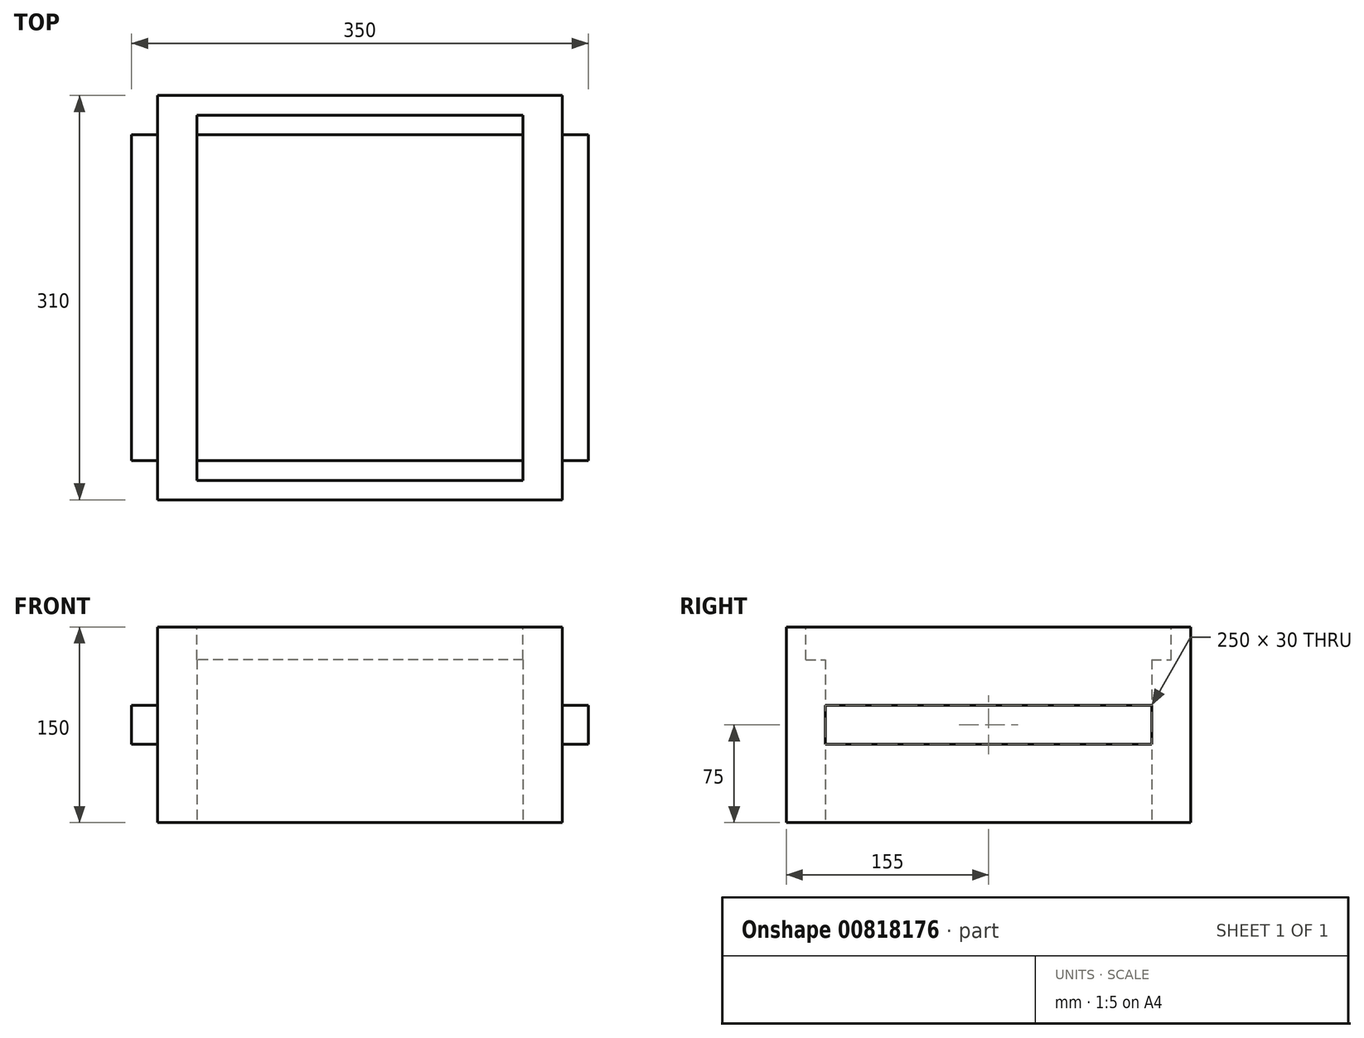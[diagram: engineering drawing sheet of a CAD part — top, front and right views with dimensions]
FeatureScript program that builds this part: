
annotation { "Feature Type Name" : "Feature", "Feature Type Description" : "" }
export const myFeature = defineFeature(function(context is Context, id is Id, definition is map)
    precondition{}
    {
        {
            var Q0;
            Q0=qCreatedBy(makeId("Top.planeOp"),FACE);
            var sketch = newSketch(context, id + "F0", { "sketchPlane" : qUnion([Q0])});
            skLineSegment(sketch, "E0.bottom", {"start": v(125, -125) * mm, "end": v(-125, -125) * mm});
            skLineSegment(sketch, "E0.top", {"start": v(125, 125) * mm, "end": v(-125, 125) * mm});
            skLineSegment(sketch, "E0.left", {"start": v(125, -125) * mm, "end": v(125, 125) * mm});
            skLineSegment(sketch, "E0.right", {"start": v(-125, -125) * mm, "end": v(-125, 125) * mm});
            skPoint(sketch, "E0.middle", {"position": v(0, 0) * mm});
            skLineSegment(sketch, "E1.bottom", {"start": v(155, -155) * mm, "end": v(-155, -155) * mm});
            skLineSegment(sketch, "E1.top", {"start": v(155, 155) * mm, "end": v(-155, 155) * mm});
            skLineSegment(sketch, "E1.left", {"start": v(155, -155) * mm, "end": v(155, 155) * mm});
            skLineSegment(sketch, "E1.right", {"start": v(-155, -155) * mm, "end": v(-155, 155) * mm});
            skSolve(sketch);
        }
        {
            var Q0;
            Q0=makeQuery(id+"F0.imprint","IMPRINT",FACE,{"disambiguationData":[TD([[makeQuery(id+"F0.imprint","IMPRINT",EDGE,{"derivedFrom":sQuery(id+"F0.wireOp",EDGE,"E0.bottom")}),1.0]])]});
            extrude(context, id + "F1", {"entities" : qUnion([Q0]), "endBound" : BoundingType.SYMMETRIC, "depth" : 150 * mm, "offsetDistance" : 25.4 * mm});
        }
        {
            var Q0;
            Q0=makeQuery(id+"F1.opExtrude","CAP_FACE",FACE,{"disambiguationData":[OSD([sQuery(id+"F0.wireOp",EDGE,"E0.bottom"),sQuery(id+"F0.wireOp",EDGE,"E0.top"),sQuery(id+"F0.wireOp",EDGE,"E0.left"),sQuery(id+"F0.wireOp",EDGE,"E0.right"),sQuery(id+"F0.wireOp",EDGE,"E1.bottom"),sQuery(id+"F0.wireOp",EDGE,"E1.top"),sQuery(id+"F0.wireOp",EDGE,"E1.left"),sQuery(id+"F0.wireOp",EDGE,"E1.right")])],"isStart":false});
            cPlane(context, id + "F2", {"entities" : qUnion([Q0]), "cplaneType" : CPlaneType.OFFSET, "offset" : 0 * mm, "width" : 152.4 * mm, "height" : 152.4 * mm});
        }
        {
            var Q0;
            Q0=qCreatedBy(id+"F2.planeOp",FACE);
            var sketch = newSketch(context, id + "F3", { "sketchPlane" : qUnion([Q0])});
            skLineSegment(sketch, "E2.bottom", {"start": v(125, -140) * mm, "end": v(-125, -140) * mm});
            skLineSegment(sketch, "E2.top", {"start": v(125, 140) * mm, "end": v(-125, 140) * mm});
            skLineSegment(sketch, "E2.left", {"start": v(125, -140) * mm, "end": v(125, 140) * mm});
            skLineSegment(sketch, "E2.right", {"start": v(-125, -140) * mm, "end": v(-125, 140) * mm});
            skPoint(sketch, "E2.middle", {"position": v(0, 0) * mm});
            skSolve(sketch);
        }
        {
            var Q0;
            Q0=makeQuery(id+"F3.imprint","IMPRINT",FACE,{"disambiguationData":[TD([[makeQuery(id+"F3.imprint","IMPRINT",EDGE,{"derivedFrom":sQuery(id+"F3.wireOp",EDGE,"E2.bottom")}),-1.0]])]});
            extrude(context, id + "F4", {"entities" : qUnion([Q0]), "operationType" : NewBodyOperationType.REMOVE, "oppositeDirection" : true, "depth" : 25 * mm, "offsetDistance" : 25 * mm});
        }
        {
            var Q0;
            Q0=makeQuery(id+"F1.opExtrude","SWEPT_FACE",FACE,{"disambiguationData":[OSD([sQuery(id+"F0.wireOp",EDGE,"E1.right")])]});
            var sketch = newSketch(context, id + "F5", { "sketchPlane" : qUnion([Q0])});
            skLineSegment(sketch, "E3.bottom", {"start": v(125, -15) * mm, "end": v(-125, -15) * mm});
            skLineSegment(sketch, "E3.top", {"start": v(125, 15) * mm, "end": v(-125, 15) * mm});
            skLineSegment(sketch, "E3.left", {"start": v(125, -15) * mm, "end": v(125, 15) * mm});
            skLineSegment(sketch, "E3.right", {"start": v(-125, -15) * mm, "end": v(-125, 15) * mm});
            skPoint(sketch, "E3.middle", {"position": v(0, 0) * mm});
            skSolve(sketch);
        }
        {
            var Q0;
            Q0=makeQuery(id+"F5.imprint","IMPRINT",FACE,{"disambiguationData":[TD([[makeQuery(id+"F5.imprint","IMPRINT",EDGE,{"derivedFrom":sQuery(id+"F5.wireOp",EDGE,"E3.bottom")}),-1.0]])]});
            extrude(context, id + "F6", {"entities" : qUnion([Q0]), "operationType" : NewBodyOperationType.ADD, "depth" : 20 * mm, "offsetDistance" : 25 * mm});
        }
        {
            var Q0;
            Q0=makeQuery(id+"F1.opExtrude","SWEPT_FACE",FACE,{"disambiguationData":[OSD([sQuery(id+"F0.wireOp",EDGE,"E1.left")])]});
            var sketch = newSketch(context, id + "F7", { "sketchPlane" : qUnion([Q0])});
            skLineSegment(sketch, "E4.bottom", {"start": v(125, -15) * mm, "end": v(-125, -15) * mm});
            skLineSegment(sketch, "E4.top", {"start": v(125, 15) * mm, "end": v(-125, 15) * mm});
            skLineSegment(sketch, "E4.left", {"start": v(125, -15) * mm, "end": v(125, 15) * mm});
            skLineSegment(sketch, "E4.right", {"start": v(-125, -15) * mm, "end": v(-125, 15) * mm});
            skPoint(sketch, "E4.middle", {"position": v(0, 0) * mm});
            skSolve(sketch);
        }
        {
            var Q0;
            Q0 = qSketchRegion(id + "F7", true);
            extrude(context, id + "F8", {"entities" : qUnion([Q0]), "operationType" : NewBodyOperationType.ADD, "depth" : 20 * mm, "offsetDistance" : 25 * mm});
        }
    });
